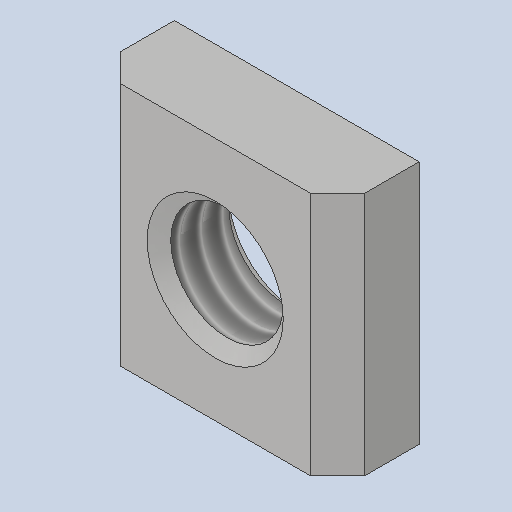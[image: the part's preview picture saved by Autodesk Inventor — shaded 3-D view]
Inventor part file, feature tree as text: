
AUTODESK INVENTOR PART (.ipt)
format: ipt  version: 2022 (Build 260153000, 153)  size: 143,360 bytes
history: native  units: mm
features: sketch x3, extrude x2, revolve x1, thread x1, plane x1
ambient origin geometry x8: Origin, YZ Plane, XZ Plane, XY Plane, X Axis, Y Axis, Z Axis, Center Point
bodies: Solid1 (feature_tree)
feature tree (8):
  extrude  "Extrusion1"  TaperAngle=360.0deg  [1 undecoded]
  revolve  "Revolution1"  [1 undecoded]
  thread  "Thread1"  [1 undecoded]
  extrude  "Extrusion2"  [1 undecoded]
  plane  "Work Plane1"
  sketch  "Sketch_1"  dims[d0=3.0mm d1=0.0mm d2=360.0deg]
  sketch  "Sketch_2"  dims[d3=2.134mm d4=0.0mm d5=18.0mm d6=0.0mm]
  sketch  "Sketch_3"
note: 4 required parameter values undecoded (feature->parameter linkage not recoverable at this tier; creation-order binding heuristic only, values carry confidence <= 0.55)